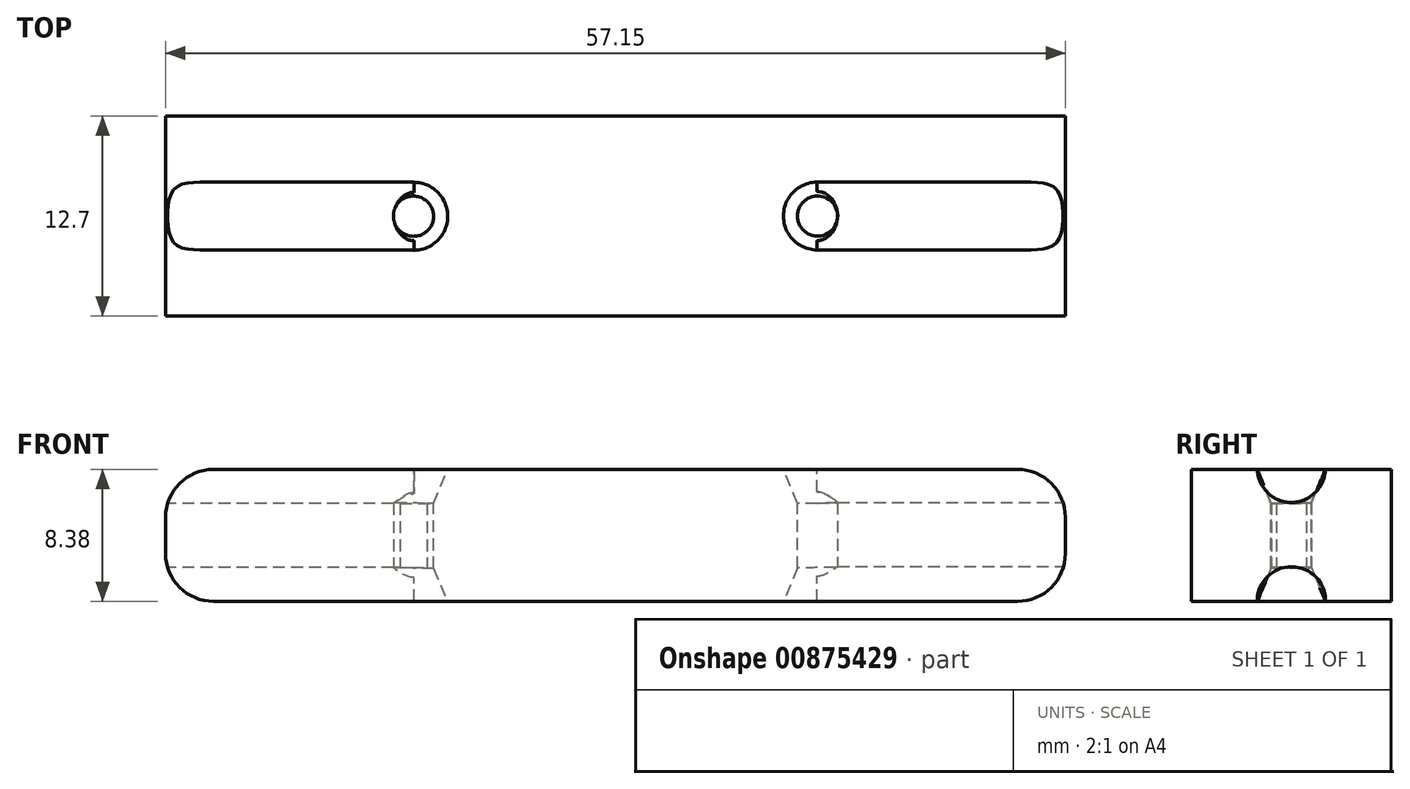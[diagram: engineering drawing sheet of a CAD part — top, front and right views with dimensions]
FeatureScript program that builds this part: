
annotation { "Feature Type Name" : "Feature", "Feature Type Description" : "" }
export const myFeature = defineFeature(function(context is Context, id is Id, definition is map)
    precondition{}
    {
        {
            var Q0;
            Q0=qCreatedBy(makeId("Front.planeOp"),FACE);
            var sketch = newSketch(context, id + "F0", { "sketchPlane" : qUnion([Q0])});
            skLineSegment(sketch, "E0.bottom", {"start": v(-21.03, 5.22) * mm, "end": v(36.12, 5.22) * mm});
            skLineSegment(sketch, "E0.top", {"start": v(-21.03, -3.16) * mm, "end": v(36.12, -3.16) * mm});
            skLineSegment(sketch, "E0.left", {"start": v(-21.03, 5.22) * mm, "end": v(-21.03, -3.16) * mm});
            skLineSegment(sketch, "E0.right", {"start": v(36.12, 5.22) * mm, "end": v(36.12, -3.16) * mm});
            skSolve(sketch);
        }
        {
            var Q0;
            Q0=makeQuery(id+"F0.imprint","IMPRINT",FACE,{"disambiguationData":[TD([[makeQuery(id+"F0.imprint","IMPRINT",EDGE,{"derivedFrom":sQuery(id+"F0.wireOp",EDGE,"E0.bottom")}),-1.0]])]});
            extrude(context, id + "F1", {"entities" : qUnion([Q0]), "depth" : 6.35 * mm, "offsetDistance" : 25.4 * mm, "hasSecondDirection" : true, "secondDirectionOppositeDirection" : true, "secondDirectionDepth" : 6.35 * mm});
        }
        {
            var Q0;
            Q0=makeQuery(id+"F1.opExtrude","SWEPT_EDGE",EDGE,{"disambiguationData":[OSD([sQuery(id+"F0.wireOp",EDGE,"E0.bottom"),sQuery(id+"F0.wireOp",EDGE,"E0.left")])]});
            var Q1;
            Q1=makeQuery(id+"F1.opExtrude","SWEPT_EDGE",EDGE,{"disambiguationData":[OSD([sQuery(id+"F0.wireOp",EDGE,"E0.bottom"),sQuery(id+"F0.wireOp",EDGE,"E0.right")])]});
            var Q2;
            Q2=makeQuery(id+"F1.opExtrude","SWEPT_EDGE",EDGE,{"disambiguationData":[OSD([sQuery(id+"F0.wireOp",EDGE,"E0.top"),sQuery(id+"F0.wireOp",EDGE,"E0.left")])]});
            var Q3;
            Q3=makeQuery(id+"F1.opExtrude","SWEPT_EDGE",EDGE,{"disambiguationData":[OSD([sQuery(id+"F0.wireOp",EDGE,"E0.top"),sQuery(id+"F0.wireOp",EDGE,"E0.right")])]});
            fillet(context, id + "F2", {"entities" : qUnion([Q0, Q1, Q2, Q3]), "radius" : 3.05 * mm, "tangentPropagation" : true, "allowEdgeOverflow" : false});
        }
        {
            var Q0;
            Q0=makeQuery(id+"F1.opExtrude","SWEPT_FACE",FACE,{"disambiguationData":[OSD([sQuery(id+"F0.wireOp",EDGE,"E0.bottom")])]});
            var sketch = newSketch(context, id + "F3", { "sketchPlane" : qUnion([Q0])});
            skCircle(sketch, "E1", {"center": v(-5.28, -0.02) * mm, "radius": 1.3 * mm});
            skPoint(sketch, "E1.centerSnap0", {"position": v(-5.28, -0.02) * mm});
            skCircle(sketch, "E2", {"center": v(20.37, 0) * mm, "radius": 1.3 * mm});
            skSolve(sketch);
        }
        {
            var Q0;
            Q0=makeQuery(id+"F1.opExtrude","SWEPT_FACE",FACE,{"disambiguationData":[OSD([sQuery(id+"F0.wireOp",EDGE,"E0.top")])]});
            var sketch = newSketch(context, id + "F4", { "sketchPlane" : qUnion([Q0])});
            skCircle(sketch, "E3", {"center": v(-5.3, 0) * mm, "radius": 1.32 * mm});
            skCircle(sketch, "E4", {"center": v(20.38, 0) * mm, "radius": 1.3 * mm});
            skSolve(sketch);
        }
        {
            var Q0;
            Q0=sQuery(id+"F3.wireOp",VERTEX,"E1.centerSnap0");
            var Q1;
            Q1=sQuery(id+"F3.wireOp",VERTEX,"E2.center");
            var Q2;
            Q2=sQuery(id+"F4.wireOp",VERTEX,"E4.center");
            var Q3;
            Q3=sQuery(id+"F4.wireOp",VERTEX,"E3.center");
            var Q4;
            Q4=makeQuery(id+"F1.opExtrude","SWEPT_BODY",BODY,{"disambiguationData":[OSD([sQuery(id+"F0.wireOp",EDGE,"E0.bottom"),sQuery(id+"F0.wireOp",EDGE,"E0.top"),sQuery(id+"F0.wireOp",EDGE,"E0.left"),sQuery(id+"F0.wireOp",EDGE,"E0.right")])]});
            hole(context, id + "F5", {"style" : HoleStyle.C_SINK, "endStyle" : HoleEndStyle.THROUGH, "holeDiameter" : 2.54 * mm, "cSinkDiameter" : 4.32 * mm, "cSinkAngle" : 45 * degree, "majorDiameter" : 6.35 * mm, "isTappedThrough" : true, "tappedDepth" : 12.7 * mm, "tapClearance" : 3, "locations" : qUnion([Q0, Q1, Q2, Q3]), "scope" : qUnion([Q4])});
        }
        {
            var Q0;
            Q0=makeQuery(id+"F1.opExtrude","SWEPT_FACE",FACE,{"disambiguationData":[OSD([sQuery(id+"F0.wireOp",EDGE,"E0.left")])]});
            var sketch = newSketch(context, id + "F6", { "sketchPlane" : qUnion([Q0])});
            skCircle(sketch, "E5", {"center": v(0, 5.23) * mm, "radius": 2.16 * mm});
            skCircle(sketch, "E6", {"center": v(0, -3.16) * mm, "radius": 2.16 * mm});
            skSolve(sketch);
        }
        {
            var Q0;
            Q0=makeQuery(id+"F1.opExtrude","SWEPT_FACE",FACE,{"disambiguationData":[OSD([sQuery(id+"F0.wireOp",EDGE,"E0.right")])]});
            var sketch = newSketch(context, id + "F7", { "sketchPlane" : qUnion([Q0])});
            skCircle(sketch, "E7", {"center": v(0, 5.28) * mm, "radius": 2.16 * mm});
            skCircle(sketch, "E8", {"center": v(0, -3.12) * mm, "radius": 2.17 * mm});
            skSolve(sketch);
        }
        {
            var Q0;
            Q0=makeQuery(id+"F7.imprint","IMPRINT",FACE,{"disambiguationData":[TD([[makeQuery(id+"F7.imprint","IMPRINT",EDGE,{"derivedFrom":sQuery(id+"F7.wireOp",EDGE,"E7")}),1.0]])]});
            var Q1;
            Q1=makeQuery(id+"F7.imprint","IMPRINT",FACE,{"disambiguationData":[TD([[makeQuery(id+"F7.imprint","IMPRINT",EDGE,{"derivedFrom":sQuery(id+"F7.wireOp",EDGE,"E8")}),1.0]])]});
            extrude(context, id + "F8", {"entities" : qUnion([Q0, Q1]), "operationType" : NewBodyOperationType.REMOVE, "oppositeDirection" : true, "depth" : 15.78 * mm, "offsetDistance" : 25.4 * mm});
        }
        {
            var Q0;
            Q0=makeQuery(id+"F6.imprint","IMPRINT",FACE,{"disambiguationData":[TD([[makeQuery(id+"F6.imprint","IMPRINT",EDGE,{"derivedFrom":sQuery(id+"F6.wireOp",EDGE,"E5")}),1.0]])]});
            var Q1;
            Q1=makeQuery(id+"F6.imprint","IMPRINT",FACE,{"disambiguationData":[TD([[makeQuery(id+"F6.imprint","IMPRINT",EDGE,{"derivedFrom":sQuery(id+"F6.wireOp",EDGE,"E6")}),1.0]])]});
            extrude(context, id + "F9", {"entities" : qUnion([Q0, Q1]), "operationType" : NewBodyOperationType.REMOVE, "oppositeDirection" : true, "depth" : 15.77 * mm, "offsetDistance" : 25.4 * mm});
        }
    });
